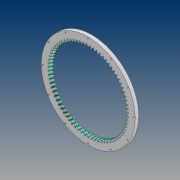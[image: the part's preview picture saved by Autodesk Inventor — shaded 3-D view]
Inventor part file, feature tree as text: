
AUTODESK INVENTOR PART (.ipt)
format: ipt  version: 2021 (Build 250183000, 183)  size: 1,977,856 bytes
history: native  units: in
note: dims shown in document units (in); Inventor stores cm internally (conversion verified against a paired STEP export)
features: extrude x2, sketch x2, thread x1, pattern_circular x1
ambient origin geometry x8: Origin, YZ Plane, XZ Plane, XY Plane, X Axis, Y Axis, Z Axis, Center Point
bodies: Solid2 (feature_tree), Solid1 (feature_tree)
feature tree (6):
  extrude  "Extrusion9"  Depth=0.3937in TaperAngle=0.0deg
  extrude  "Extrusion10"  Depth=1.1022in
  thread  "Thread27"  [1 undecoded]
  pattern_circular  "Circular Pattern10"  [2 undecoded]
  sketch  "Sketch9"  dims[d118=28.6013in d119=0.3937in d120=0.0in]
  sketch  "Sketch10"  dims[d121=27.7165in d122=0.315in d123=0.0in d124=0.0in d125=1.1022in d126=0.0in d127=4.7244in d128=360.0deg]
note: 3 required parameter values undecoded (feature->parameter linkage not recoverable at this tier; creation-order binding heuristic only, values carry confidence <= 0.55)
